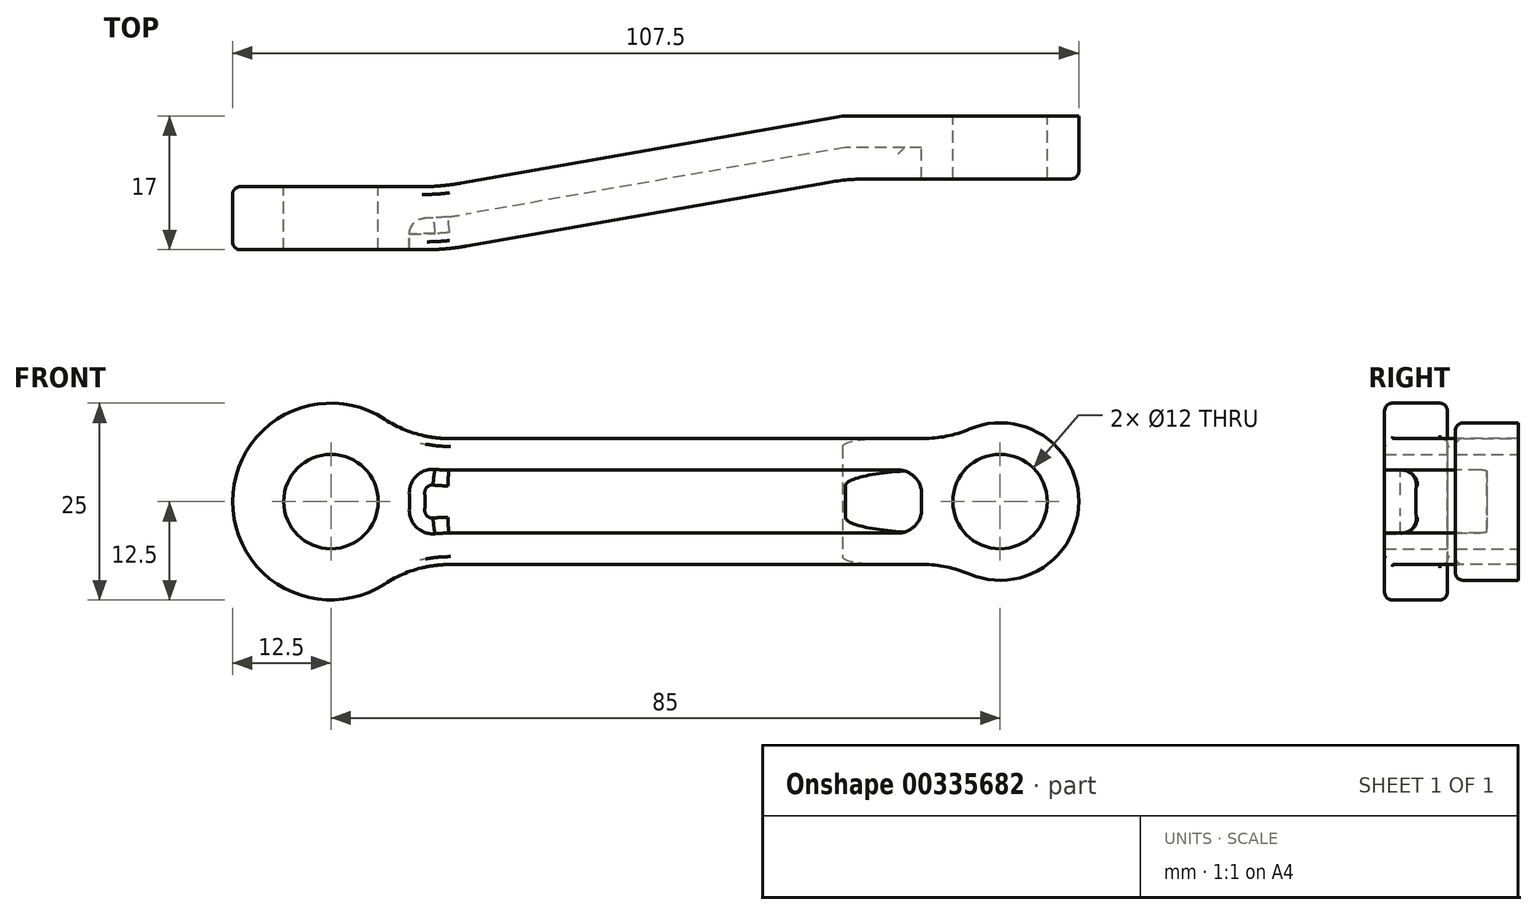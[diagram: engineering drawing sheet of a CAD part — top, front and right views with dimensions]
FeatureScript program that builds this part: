
annotation { "Feature Type Name" : "Feature", "Feature Type Description" : "" }
export const myFeature = defineFeature(function(context is Context, id is Id, definition is map)
    precondition{}
    {
        {
            var Q0;
            Q0=qCreatedBy(makeId("Front.planeOp"),FACE);
            var sketch = newSketch(context, id + "F0", { "sketchPlane" : qUnion([Q0])});
            skCircle(sketch, "E0", {"center": v(0, 0) * mm, "radius": 10 * mm});
            skCircle(sketch, "E1", {"center": v(-85, 0) * mm, "radius": 12.5 * mm});
            skCircle(sketch, "E2", {"center": v(-85, 0) * mm, "radius": 6 * mm});
            skCircle(sketch, "E3", {"center": v(0, 0) * mm, "radius": 6 * mm});
            skLineSegment(sketch, "E4", {"start": v(-85, 0) * mm, "end": v(0, 0) * mm, "construction": true});
            skLineSegment(sketch, "E5", {"start": v(-75.4, 8) * mm, "end": v(-6, 8) * mm});
            skLineSegment(sketch, "E6", {"start": v(-75.4, -8) * mm, "end": v(-6, -8) * mm});
            skSolve(sketch);
        }
        {
            var Q0;
            Q0=makeQuery(id+"F0.imprint","IMPRINT",FACE,{"disambiguationData":[TD([[makeQuery(id+"F0.imprint","IMPRINT",EDGE,{"derivedFrom":sQuery(id+"F0.wireOp",EDGE,"E2")}),-1.0]])]});
            var Q1;
            {var subQ0=sQuery(id+"F0.wireOp",EDGE,"E5");Q1=makeQuery(id+"F0.imprint","IMPRINT",FACE,{"disambiguationData":[TD([[makeQuery(id+"F0.imprint","IMPRINT",EDGE,{"derivedFrom":subQ0}),-1.0]])]});}
            var Q2;
            Q2=makeQuery(id+"F0.imprint","IMPRINT",FACE,{"disambiguationData":[TD([[makeQuery(id+"F0.imprint","IMPRINT",EDGE,{"derivedFrom":sQuery(id+"F0.wireOp",EDGE,"E3")}),-1.0]])]});
            extrude(context, id + "F1", {"entities" : qUnion([Q0, Q1, Q2]), "depth" : 25 * mm});
        }
        {
            var Q0;
            Q0=qCreatedBy(makeId("Top.planeOp"),FACE);
            var sketch = newSketch(context, id + "F2", { "sketchPlane" : qUnion([Q0])});
            skLineSegment(sketch, "E7", {"start": v(-110.22, -9) * mm, "end": v(-71.04, -9) * mm});
            skLineSegment(sketch, "E8", {"start": v(-71.04, -9) * mm, "end": v(-20, 0) * mm});
            skLineSegment(sketch, "E9", {"start": v(-20, 0) * mm, "end": v(29.22, 0) * mm});
            skLineSegment(sketch, "E10", {"start": v(29.22, 0) * mm, "end": v(29.22, -8) * mm});
            skLineSegment(sketch, "E11", {"start": v(29.22, -8) * mm, "end": v(-19.3, -8) * mm});
            skLineSegment(sketch, "E12", {"start": v(-19.3, -8) * mm, "end": v(-70.34, -17) * mm});
            skLineSegment(sketch, "E13", {"start": v(-70.34, -17) * mm, "end": v(-110.22, -17) * mm});
            skLineSegment(sketch, "E14", {"start": v(-110.22, -17) * mm, "end": v(-110.22, -9) * mm});
            skSolve(sketch);
        }
        {
            var Q0;
            Q0=makeQuery(id+"F2.imprint","IMPRINT",FACE,{"disambiguationData":[TD([[makeQuery(id+"F2.imprint","IMPRINT",EDGE,{"derivedFrom":sQuery(id+"F2.wireOp",EDGE,"E7")}),-1.0]])]});
            extrude(context, id + "F3", {"entities" : qUnion([Q0]), "operationType" : NewBodyOperationType.INTERSECT, "endBound" : BoundingType.SYMMETRIC, "depth" : 40 * mm});
        }
        {
            var Q0;
            Q0=makeQuery(id+"F3.boolean.opBoolean","COPY",EDGE,{"derivedFrom":makeQuery(id+"F3.opExtrude","SWEPT_EDGE",EDGE,{"disambiguationData":[OSD([sQuery(id+"F2.wireOp",EDGE,"E12"),sQuery(id+"F2.wireOp",EDGE,"E13")])]})});
            var Q1;
            Q1=makeQuery(id+"F3.boolean.opBoolean","COPY",EDGE,{"derivedFrom":makeQuery(id+"F3.opExtrude","SWEPT_EDGE",EDGE,{"disambiguationData":[OSD([sQuery(id+"F2.wireOp",EDGE,"E11"),sQuery(id+"F2.wireOp",EDGE,"E12")])]})});
            var Q2;
            Q2=makeQuery(id+"F3.boolean.opBoolean","COPY",EDGE,{"derivedFrom":makeQuery(id+"F3.opExtrude","SWEPT_EDGE",EDGE,{"disambiguationData":[OSD([sQuery(id+"F2.wireOp",EDGE,"E8"),sQuery(id+"F2.wireOp",EDGE,"E9")])]})});
            var Q3;
            Q3=makeQuery(id+"F3.boolean.opBoolean","COPY",EDGE,{"derivedFrom":makeQuery(id+"F3.opExtrude","SWEPT_EDGE",EDGE,{"disambiguationData":[OSD([sQuery(id+"F2.wireOp",EDGE,"E7"),sQuery(id+"F2.wireOp",EDGE,"E8")])]})});
            fillet(context, id + "F4", {"entities" : qUnion([Q0, Q1, Q2, Q3]), "radius" : 30 * mm, "tangentPropagation" : true, "allowEdgeOverflow" : false});
        }
        {
            var Q0;
            Q0=makeQuery(id+"F1.opExtrude","SWEPT_EDGE",EDGE,{"disambiguationData":[OSD([sQuery(id+"F0.wireOp",EDGE,"E1"),sQuery(id+"F0.wireOp",EDGE,"E5")])]});
            var Q1;
            Q1=makeQuery(id+"F1.opExtrude","SWEPT_EDGE",EDGE,{"disambiguationData":[OSD([sQuery(id+"F0.wireOp",EDGE,"E0"),sQuery(id+"F0.wireOp",EDGE,"E5")])]});
            var Q2;
            Q2=makeQuery(id+"F1.opExtrude","SWEPT_EDGE",EDGE,{"disambiguationData":[OSD([sQuery(id+"F0.wireOp",EDGE,"E1"),sQuery(id+"F0.wireOp",EDGE,"E6")])]});
            var Q3;
            Q3=makeQuery(id+"F1.opExtrude","SWEPT_EDGE",EDGE,{"disambiguationData":[OSD([sQuery(id+"F0.wireOp",EDGE,"E0"),sQuery(id+"F0.wireOp",EDGE,"E6")])]});
            fillet(context, id + "F5", {"entities" : qUnion([Q0, Q1, Q2, Q3]), "radius" : 15 * mm, "tangentPropagation" : true, "allowEdgeOverflow" : false});
        }
        {
            var Q0;
            Q0=makeQuery(id+"F3.boolean.opBoolean","COPY",FACE,{"derivedFrom":makeQuery(id+"F3.opExtrude","SWEPT_FACE",FACE,{"disambiguationData":[OSD([sQuery(id+"F2.wireOp",EDGE,"E11")])]})});
            var Q1;
            Q1=makeQuery(id+"F4.opFillet","BLEND_FACE",FACE,{"disambiguationData":[OSD([sQuery(id+"F2.wireOp",EDGE,"E11"),sQuery(id+"F2.wireOp",EDGE,"E12")])]});
            var Q2;
            Q2=makeQuery(id+"F3.boolean.opBoolean","COPY",FACE,{"derivedFrom":makeQuery(id+"F3.opExtrude","SWEPT_FACE",FACE,{"disambiguationData":[OSD([sQuery(id+"F2.wireOp",EDGE,"E12")])]})});
            var Q3;
            Q3=makeQuery(id+"F4.opFillet","BLEND_FACE",FACE,{"disambiguationData":[OSD([sQuery(id+"F2.wireOp",EDGE,"E12"),sQuery(id+"F2.wireOp",EDGE,"E13")])]});
            var Q4;
            Q4=makeQuery(id+"F3.boolean.opBoolean","COPY",FACE,{"derivedFrom":makeQuery(id+"F3.opExtrude","SWEPT_FACE",FACE,{"disambiguationData":[OSD([sQuery(id+"F2.wireOp",EDGE,"E13")])]})});
            shell(context, id + "F6", {"entities" : qUnion([Q0, Q1, Q2, Q3, Q4]), "thickness" : 4 * mm});
        }
        {
            var Q0;
            Q0=makeQuery(id+"F6.opShell","TWEAK_EDGE",EDGE,{"derivedFrom":[makeQuery(id+"F1.opExtrude","SWEPT_FACE",FACE,{"disambiguationData":[OSD([sQuery(id+"F0.wireOp",EDGE,"E3")])]}),makeQuery(id+"F5.opFillet","BLEND_FACE",FACE,{"disambiguationData":[OSD([sQuery(id+"F0.wireOp",EDGE,"E0"),sQuery(id+"F0.wireOp",EDGE,"E5")])]})]});
            var Q1;
            Q1=makeQuery(id+"F6.opShell","TWEAK_EDGE",EDGE,{"derivedFrom":[makeQuery(id+"F1.opExtrude","SWEPT_FACE",FACE,{"disambiguationData":[OSD([sQuery(id+"F0.wireOp",EDGE,"E3")])]}),makeQuery(id+"F5.opFillet","BLEND_FACE",FACE,{"disambiguationData":[OSD([sQuery(id+"F0.wireOp",EDGE,"E0"),sQuery(id+"F0.wireOp",EDGE,"E6")])]})]});
            var Q2;
            Q2=makeQuery(id+"F6.opShell","TWEAK_EDGE",EDGE,{"derivedFrom":[makeQuery(id+"F1.opExtrude","SWEPT_FACE",FACE,{"disambiguationData":[OSD([sQuery(id+"F0.wireOp",EDGE,"E2")])]}),makeQuery(id+"F5.opFillet","BLEND_FACE",FACE,{"disambiguationData":[OSD([sQuery(id+"F0.wireOp",EDGE,"E1"),sQuery(id+"F0.wireOp",EDGE,"E5")])]})]});
            var Q3;
            Q3=makeQuery(id+"F6.opShell","TWEAK_EDGE",EDGE,{"derivedFrom":[makeQuery(id+"F1.opExtrude","SWEPT_FACE",FACE,{"disambiguationData":[OSD([sQuery(id+"F0.wireOp",EDGE,"E2")])]}),makeQuery(id+"F5.opFillet","BLEND_FACE",FACE,{"disambiguationData":[OSD([sQuery(id+"F0.wireOp",EDGE,"E1"),sQuery(id+"F0.wireOp",EDGE,"E6")])]})]});
            fillet(context, id + "F7", {"entities" : qUnion([Q0, Q1, Q2, Q3]), "radius" : 3 * mm, "tangentPropagation" : true, "allowEdgeOverflow" : false});
        }
        {
            var Q0;
            Q0=makeQuery(id+"F6.opShell","OFFSET_EDGE",EDGE,{"disambiguationData":[OSD([sQuery(id+"F0.wireOp",EDGE,"E6"),sQuery(id+"F2.wireOp",EDGE,"E8")])]});
            fillet(context, id + "F8", {"entities" : qUnion([Q0]), "radius" : 2 * mm, "tangentPropagation" : true, "allowEdgeOverflow" : false});
        }
        {
            var Q0;
            Q0=makeQuery(id+"F3.boolean.opBoolean","INTERSECT",EDGE,{"derivedFrom":[makeQuery(id+"F1.opExtrude","SWEPT_FACE",FACE,{"disambiguationData":[OSD([sQuery(id+"F0.wireOp",EDGE,"E5")])]}),makeQuery(id+"F3.opExtrude","SWEPT_FACE",FACE,{"disambiguationData":[OSD([sQuery(id+"F2.wireOp",EDGE,"E12")])]})]});
            var Q1;
            Q1=makeQuery(id+"F3.boolean.opBoolean","INTERSECT",EDGE,{"derivedFrom":[makeQuery(id+"F1.opExtrude","SWEPT_FACE",FACE,{"disambiguationData":[OSD([sQuery(id+"F0.wireOp",EDGE,"E5")])]}),makeQuery(id+"F3.opExtrude","SWEPT_FACE",FACE,{"disambiguationData":[OSD([sQuery(id+"F2.wireOp",EDGE,"E8")])]})]});
            fillet(context, id + "F9", {"entities" : qUnion([Q0, Q1]), "radius" : 1 * mm, "tangentPropagation" : true, "allowEdgeOverflow" : false});
        }
    });
